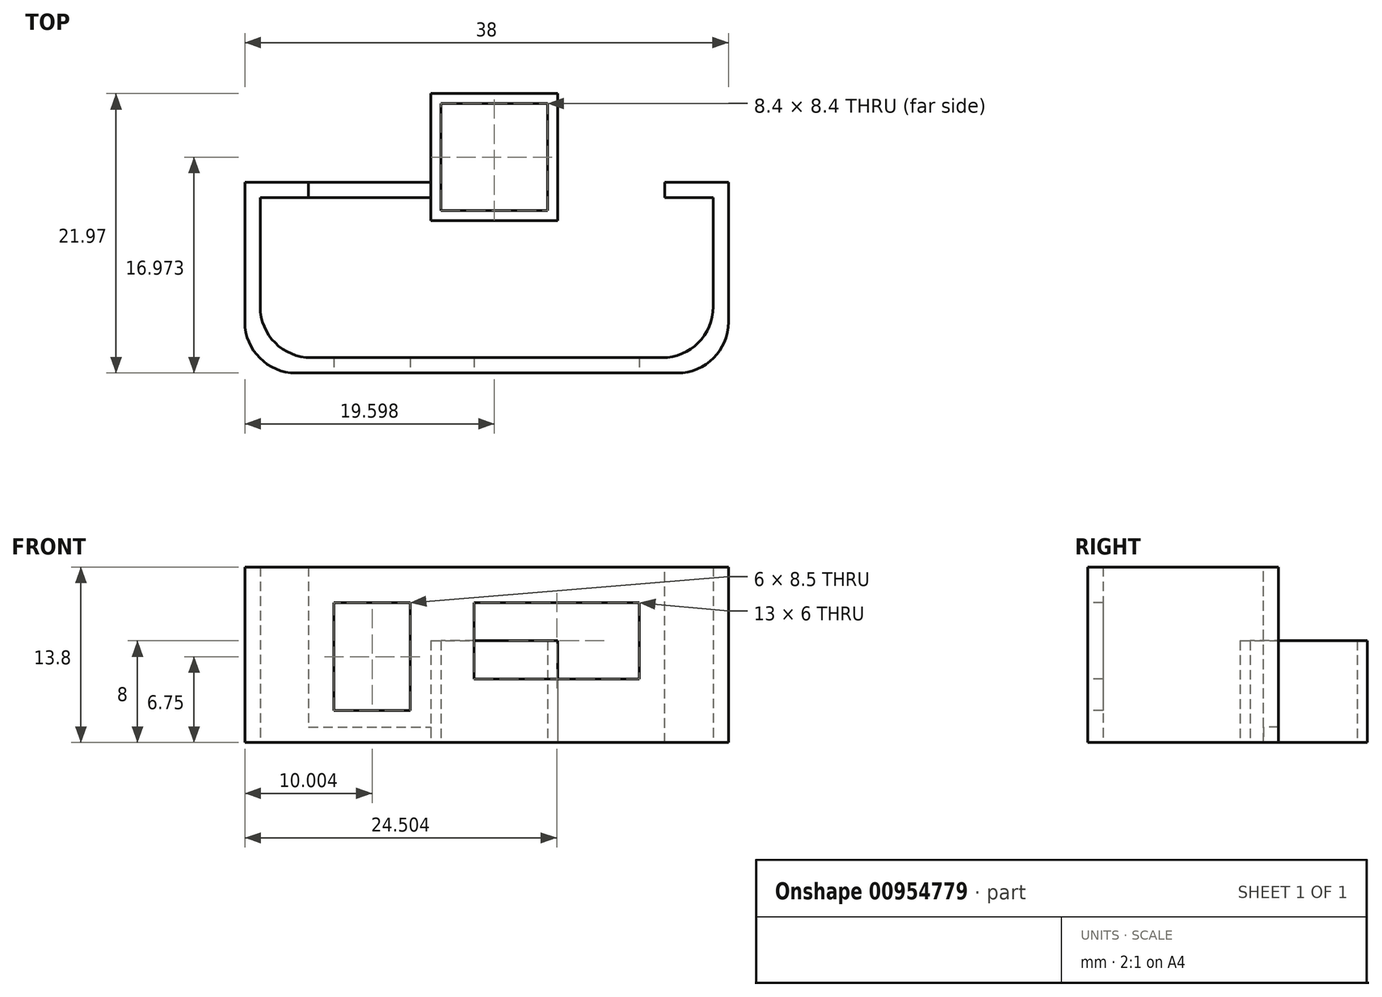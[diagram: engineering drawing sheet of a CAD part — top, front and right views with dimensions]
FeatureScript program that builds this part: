
annotation { "Feature Type Name" : "Feature", "Feature Type Description" : "" }
export const myFeature = defineFeature(function(context is Context, id is Id, definition is map)
    precondition{}
    {
        {
            var Q0;
            Q0=qCreatedBy(makeId("Top.planeOp"),FACE);
            var sketch = newSketch(context, id + "F0", { "sketchPlane" : qUnion([Q0])});
            skLineSegment(sketch, "E0.bottom", {"start": v(-53.66, 7.5) * mm, "end": v(-15.66, 7.5) * mm});
            skLineSegment(sketch, "E0.top", {"start": v(-53.66, -7.5) * mm, "end": v(-15.66, -7.5) * mm});
            skLineSegment(sketch, "E0.left", {"start": v(-53.66, 7.5) * mm, "end": v(-53.66, -7.5) * mm});
            skLineSegment(sketch, "E0.right", {"start": v(-15.66, 7.5) * mm, "end": v(-15.66, -7.5) * mm});
            skPoint(sketch, "E1", {"position": v(-15.66, 0) * mm});
            skSolve(sketch);
        }
        {
            var Q0;
            Q0 = qSketchRegion(id + "F0", true);
            extrude(context, id + "F1", {"entities" : qUnion([Q0]), "depth" : 15 * mm, "offsetDistance" : 25 * mm});
        }
        {
            var Q0;
            Q0=makeQuery(id+"F1.opExtrude","SWEPT_FACE",FACE,{"disambiguationData":[OSD([sQuery(id+"F0.wireOp",EDGE,"E0.top")])]});
            var Q1;
            Q1=makeQuery(id+"F1.opExtrude","SWEPT_BODY",BODY,{"disambiguationData":[OSD([sQuery(id+"F0.wireOp",EDGE,"E0.bottom"),sQuery(id+"F0.wireOp",EDGE,"E0.top"),sQuery(id+"F0.wireOp",EDGE,"E0.left"),sQuery(id+"F0.wireOp",EDGE,"E0.right")])]});
            shell(context, id + "F2", {"isHollow" : true, "entities" : qUnion([Q0]), "parts" : qUnion([Q1]), "thickness" : 1.2 * mm});
        }
        {
            var Q0;
            Q0=makeQuery(id+"F1.opExtrude","SWEPT_FACE",FACE,{"disambiguationData":[OSD([sQuery(id+"F0.wireOp",EDGE,"E0.top")])]});
            var sketch = newSketch(context, id + "F3", { "sketchPlane" : qUnion([Q0])});
            skLineSegment(sketch, "E2.bottom", {"start": v(-35.66, 11) * mm, "end": v(-22.66, 11) * mm});
            skLineSegment(sketch, "E2.top", {"start": v(-35.66, 5) * mm, "end": v(-22.66, 5) * mm});
            skLineSegment(sketch, "E2.left", {"start": v(-35.66, 11) * mm, "end": v(-35.66, 5) * mm});
            skLineSegment(sketch, "E2.right", {"start": v(-22.66, 11) * mm, "end": v(-22.66, 5) * mm});
            skLineSegment(sketch, "E3.bottom", {"start": v(-46.66, 11) * mm, "end": v(-40.66, 11) * mm});
            skLineSegment(sketch, "E3.top", {"start": v(-46.66, 2.5) * mm, "end": v(-40.66, 2.5) * mm});
            skLineSegment(sketch, "E3.left", {"start": v(-46.66, 11) * mm, "end": v(-46.66, 2.5) * mm});
            skLineSegment(sketch, "E3.right", {"start": v(-40.66, 11) * mm, "end": v(-40.66, 2.5) * mm});
            skLineSegment(sketch, "E4", {"start": v(-22.66, 8.65) * mm, "end": v(-15.66, 8.65) * mm, "construction": true});
            skLineSegment(sketch, "E5", {"start": v(-46.66, 6.75) * mm, "end": v(-53.66, 6.75) * mm, "construction": true});
            skSolve(sketch);
        }
        {
            var Q0;
            Q0 = qSketchRegion(id + "F3", true);
            extrude(context, id + "F4", {"entities" : qUnion([Q0]), "operationType" : NewBodyOperationType.REMOVE, "endBound" : BoundingType.UP_TO_NEXT, "oppositeDirection" : true, "depth" : 25 * mm, "offsetDistance" : 25 * mm});
        }
        {
            var Q0;
            Q0=makeQuery(id+"F1.opExtrude","CAP_FACE",FACE,{"disambiguationData":[OSD([sQuery(id+"F0.wireOp",EDGE,"E0.bottom"),sQuery(id+"F0.wireOp",EDGE,"E0.top"),sQuery(id+"F0.wireOp",EDGE,"E0.left"),sQuery(id+"F0.wireOp",EDGE,"E0.right")])],"isStart":false});
            var Q1;
            {var subQ0=sQuery(id+"F0.wireOp",EDGE,"E0.right");var subQ1=sQuery(id+"F0.wireOp",EDGE,"E0.left");var subQ2=sQuery(id+"F0.wireOp",EDGE,"E0.top");var subQ3=sQuery(id+"F0.wireOp",EDGE,"E0.bottom");Q1=makeQuery(id+"F2.opShell","OFFSET_FACE",FACE,{"disambiguationData":[OSD([subQ3,subQ2,subQ1,subQ0]),TDD([makeQuery(id+"F1.opExtrude","CAP_FACE",FACE,{"disambiguationData":[OSD([subQ3,subQ2,subQ1,subQ0])],"isStart":false})])]});}
            extrude(context, id + "F5", {"entities" : qUnion([Q0]), "operationType" : NewBodyOperationType.REMOVE, "endBound" : BoundingType.UP_TO_SURFACE, "oppositeDirection" : true, "depth" : 25 * mm, "endBoundEntityFace" : qUnion([Q1]), "offsetDistance" : 25 * mm});
        }
        {
            var Q0;
            {var subQ0=sQuery(id+"F0.wireOp",EDGE,"E0.right");var subQ1=sQuery(id+"F0.wireOp",EDGE,"E0.left");var subQ2=sQuery(id+"F0.wireOp",EDGE,"E0.top");var subQ3=sQuery(id+"F0.wireOp",EDGE,"E0.bottom");Q0=makeQuery(id+"F2.opShell","OFFSET_FACE",FACE,{"disambiguationData":[OSD([subQ3,subQ2,subQ1,subQ0]),TDD([makeQuery(id+"F1.opExtrude","CAP_FACE",FACE,{"disambiguationData":[OSD([subQ3,subQ2,subQ1,subQ0])],"isStart":true})])]});}
            extrude(context, id + "F6", {"entities" : qUnion([Q0]), "operationType" : NewBodyOperationType.REMOVE, "oppositeDirection" : true, "depth" : 25 * mm, "offsetDistance" : 25 * mm});
        }
        {
            var Q0;
            Q0=makeQuery(id+"F1.opExtrude","SWEPT_EDGE",EDGE,{"disambiguationData":[OSD([sQuery(id+"F0.wireOp",EDGE,"E0.top"),sQuery(id+"F0.wireOp",EDGE,"E0.right")])]});
            var Q1;
            {var subQ0=sQuery(id+"F0.wireOp",EDGE,"E0.left");var subQ1=sQuery(id+"F0.wireOp",EDGE,"E0.top");Q1=makeQuery(id+"F6.boolean.opBoolean","MERGE",EDGE,{"derivedFrom":[makeQuery(id+"F2.opShell","OFFSET_EDGE",EDGE,{"disambiguationData":[OSD([subQ1,subQ0])]})],"fromTools":[makeQuery(id+"F6.opExtrude","SWEPT_EDGE",EDGE,{"disambiguationData":[OSD([subQ1,subQ0])]})]});}
            var Q2;
            Q2=makeQuery(id+"F1.opExtrude","SWEPT_EDGE",EDGE,{"disambiguationData":[OSD([sQuery(id+"F0.wireOp",EDGE,"E0.top"),sQuery(id+"F0.wireOp",EDGE,"E0.left")])]});
            var Q3;
            {var subQ0=sQuery(id+"F0.wireOp",EDGE,"E0.right");var subQ1=sQuery(id+"F0.wireOp",EDGE,"E0.top");Q3=makeQuery(id+"F6.boolean.opBoolean","MERGE",EDGE,{"derivedFrom":[makeQuery(id+"F2.opShell","OFFSET_EDGE",EDGE,{"disambiguationData":[OSD([subQ1,subQ0])]})],"fromTools":[makeQuery(id+"F6.opExtrude","SWEPT_EDGE",EDGE,{"disambiguationData":[OSD([subQ1,subQ0])]})]});}
            fillet(context, id + "F7", {"entities" : qUnion([Q0, Q1, Q2, Q3]), "radius" : 4 * mm, "tangentPropagation" : true, "allowEdgeOverflow" : false});
        }
        {
            var Q0;
            Q0=makeQuery(id+"F1.opExtrude","SWEPT_FACE",FACE,{"disambiguationData":[OSD([sQuery(id+"F0.wireOp",EDGE,"E0.bottom")])]});
            var sketch = newSketch(context, id + "F8", { "sketchPlane" : qUnion([Q0])});
            skLineSegment(sketch, "E6.bottom", {"start": v(20.66, 13.8) * mm, "end": v(48.66, 13.8) * mm});
            skLineSegment(sketch, "E6.top", {"start": v(20.66, 0) * mm, "end": v(48.66, 0) * mm});
            skLineSegment(sketch, "E6.left", {"start": v(20.66, 13.8) * mm, "end": v(20.66, 0) * mm});
            skLineSegment(sketch, "E6.right", {"start": v(48.66, 13.8) * mm, "end": v(48.66, 0) * mm});
            skSolve(sketch);
        }
        {
            var Q0;
            Q0 = qSketchRegion(id + "F8", true);
            extrude(context, id + "F9", {"entities" : qUnion([Q0]), "operationType" : NewBodyOperationType.REMOVE, "endBound" : BoundingType.UP_TO_NEXT, "oppositeDirection" : true, "depth" : 25 * mm, "offsetDistance" : 25 * mm});
        }
        {
            var Q0;
            Q0=qCreatedBy(makeId("Top.planeOp"),FACE);
            var sketch = newSketch(context, id + "F10", { "sketchPlane" : qUnion([Q0])});
            skLineSegment(sketch, "E7.bottom", {"start": v(-39.06, 4.47) * mm, "end": v(-29.06, 4.47) * mm});
            skLineSegment(sketch, "E7.top", {"start": v(-39.06, 14.47) * mm, "end": v(-29.06, 14.47) * mm});
            skLineSegment(sketch, "E7.left", {"start": v(-39.06, 4.47) * mm, "end": v(-39.06, 14.47) * mm});
            skLineSegment(sketch, "E7.right", {"start": v(-29.06, 4.47) * mm, "end": v(-29.06, 14.47) * mm});
            skSolve(sketch);
        }
        {
            var Q0;
            Q0=makeQuery(id+"F10.imprint","IMPRINT",FACE,{"disambiguationData":[TD([[makeQuery(id+"F10.imprint","IMPRINT",EDGE,{"derivedFrom":sQuery(id+"F10.wireOp",EDGE,"E7.bottom")}),1.0]])]});
            extrude(context, id + "F11", {"entities" : qUnion([Q0]), "depth" : 8 * mm, "offsetDistance" : 25 * mm});
        }
        {
            var Q0;
            Q0=makeQuery(id+"F11.opExtrude","CAP_FACE",FACE,{"disambiguationData":[OSD([sQuery(id+"F10.wireOp",EDGE,"E7.bottom"),sQuery(id+"F10.wireOp",EDGE,"E7.top"),sQuery(id+"F10.wireOp",EDGE,"E7.left"),sQuery(id+"F10.wireOp",EDGE,"E7.right")])],"isStart":true});
            shell(context, id + "F12", {"entities" : qUnion([Q0]), "thickness" : 0.8 * mm});
        }
        {
            var Q0;
            Q0=makeQuery(id+"F12.opShell","OFFSET_FACE",FACE,{"disambiguationData":[OSD([sQuery(id+"F10.wireOp",EDGE,"E7.bottom"),sQuery(id+"F10.wireOp",EDGE,"E7.top"),sQuery(id+"F10.wireOp",EDGE,"E7.left"),sQuery(id+"F10.wireOp",EDGE,"E7.right")])]});
            extrude(context, id + "F13", {"entities" : qUnion([Q0]), "operationType" : NewBodyOperationType.REMOVE, "oppositeDirection" : true, "depth" : 25 * mm, "offsetDistance" : 25 * mm});
        }
        {
            var Q0;
            Q0=qCreatedBy(makeId("Top.planeOp"),FACE);
            var sketch = newSketch(context, id + "F14", { "sketchPlane" : qUnion([Q0])});
            skLineSegment(sketch, "E8.bottom", {"start": v(-48.66, 7.5) * mm, "end": v(-39.06, 7.5) * mm});
            skLineSegment(sketch, "E8.top", {"start": v(-48.66, 6.3) * mm, "end": v(-39.06, 6.3) * mm});
            skLineSegment(sketch, "E8.left", {"start": v(-48.66, 7.5) * mm, "end": v(-48.66, 6.3) * mm});
            skLineSegment(sketch, "E8.right", {"start": v(-39.06, 7.5) * mm, "end": v(-39.06, 6.3) * mm});
            skSolve(sketch);
        }
        {
            var Q0;
            Q0=makeQuery(id+"F14.imprint","IMPRINT",FACE,{"disambiguationData":[TD([[makeQuery(id+"F14.imprint","IMPRINT",EDGE,{"derivedFrom":sQuery(id+"F14.wireOp",EDGE,"E8.bottom")}),-1.0]])]});
            extrude(context, id + "F15", {"entities" : qUnion([Q0]), "operationType" : NewBodyOperationType.ADD, "depth" : 1.2 * mm, "offsetDistance" : 25 * mm});
        }
    });
